FCSTD DOCUMENT  (FreeCAD 2022.709R28846 (Git))
Label: Fresnel_Box_Neck_Template
License: Other
objects: Sketcher::SketchObject×1, PartDesign::Body×1
note: 2 computed .brp shape members not serialized (recipe doc carries the construction recipe); baked Part::Feature solids carry a one-line shape summary decoded from their .brp

FEATURE [Sketcher::SketchObject] Sketch
  ArcFitTolerance = 1e-06
  AttachmentSupport = -> [XY_Plane]
  FullyConstrained = true
  MapMode = 5
  Support = -> [XY_Plane]
  TreeRank = 11
  sketch-geometry (16):
    g0: ArcOfCircle [constr] CenterX=-18.0352 CenterY=0 CenterZ=0 NormalX=0 NormalY=0 NormalZ=1 AngleXU=0 Radius=51.9648 StartAngle=2.35619 EndAngle=3.92699
    g1: ArcOfCircle CenterX=-1.39296 CenterY=-19.4282 CenterZ=0 NormalX=0 NormalY=0 NormalZ=1 AngleXU=0 Radius=79.4404 StartAngle=0.785398 EndAngle=2.07829
    g2: ArcOfCircle CenterX=18.0352 CenterY=0 CenterZ=0 NormalX=0 NormalY=0 NormalZ=1 AngleXU=0 Radius=51.9648 StartAngle=5.49779 EndAngle=7.06858
    g3: ArcOfCircle CenterX=-1.39296 CenterY=19.4282 CenterZ=0 NormalX=0 NormalY=0 NormalZ=1 AngleXU=0 Radius=79.4404 StartAngle=4.2049 EndAngle=5.49779
    g4: LineSegment [constr] StartX=-18.0352 StartY=0 StartZ=0 EndX=18.0352 EndY=0 EndZ=0
    g5: LineSegment [constr] StartX=0 StartY=0 StartZ=0 EndX=0 EndY=60 EndZ=0
    g6: LineSegment [constr] StartX=0 StartY=0 StartZ=0 EndX=0 EndY=-60 EndZ=0
    g7: LineSegment [constr] StartX=-18.0352 StartY=0 StartZ=0 EndX=-70 EndY=0 EndZ=0
    g8: LineSegment [constr] StartX=18.0352 StartY=0 StartZ=0 EndX=70 EndY=0 EndZ=0
    g9: LineSegment StartX=-102.5 StartY=97.5 StartZ=0 EndX=102.5 EndY=97.5 EndZ=0
    g10: LineSegment StartX=102.5 StartY=97.5 StartZ=0 EndX=102.5 EndY=-97.5 EndZ=0
    g11: LineSegment StartX=102.5 StartY=-97.5 StartZ=0 EndX=-102.5 EndY=-97.5 EndZ=0
    g12: LineSegment StartX=-102.5 StartY=-97.5 StartZ=0 EndX=-102.5 EndY=-50 EndZ=0
    g13: LineSegment StartX=-40 StartY=50 StartZ=0 EndX=-102.5 EndY=50 EndZ=0
    g14: LineSegment StartX=-40 StartY=-50 StartZ=0 EndX=-102.5 EndY=-50 EndZ=0
    g15: LineSegment StartX=-102.5 StartY=50 StartZ=0 EndX=-102.5 EndY=97.5 EndZ=0
  constraints (46):
    c: Tangent(g1,g2) = -1.5708
    c: Tangent(g2,g3) = -1.5708
    c: Horizontal(g0,g2)
    c: Coincident(g4,g0)
    c: Coincident(g4,g2)
    c: PointOnObject(g5,g1)
    c: Vertical(g5)
    c: Coincident(g6,g5)
    c: PointOnObject(g6,g3)
    c: Symmetric(g0,g2,g5)
    c: Symmetric(g5,g6,g5)
    c: Equal(g2,g0)
    c: Coincident(g5,g-1)
    c: DistanceY(g6,g5) = 120
    c: Coincident(g7,g0)
    c: PointOnObject(g7,g0)
    c: Horizontal(g7)
    c: Coincident(g8,g2)
    c: PointOnObject(g8,g2)
    c: Horizontal(g8)
    c: DistanceX(g7,g8) = 140
    c: Angle(g2) = 1.5708
    c: Coincident(g9,g10)
    c: Coincident(g10,g11)
    c: Coincident(g11,g12)
    c: Coincident(g15,g9)
    c: Horizontal(g9)
    c: Horizontal(g11)
    c: Vertical(g10)
    c: Vertical(g12)
    c: DistanceX(g9,g9) = 205
    c: DistanceY(g10,g10) = 195
    c: Symmetric(g9,g10,g5)
    c: Horizontal(g13)
    c: Horizontal(g14)
    c: Symmetric(g14,g13,g-1)
    c: DistanceY(g14,g13) = 100
    c: PointOnObject(g12,g14)
    c: Coincident(g15,g13)
    c: Tangent(g12,g15)
    c: Coincident(g1,g13)
    c: Coincident(g3,g14)
    c: DistanceX(g1,g-1) = 40
    c: Equal(g14,g13)
    c: Horizontal(g0,g1)
    c: Horizontal(g0,g2)
FEATURE [PartDesign::Body] Body
  AutoGroupSolids = false
  ClaimAllChildren = false
  ExportMode = 0
  Group = -> [Sketch]
  Origin = -> Origin
  TreeRank = 10
  _ExportChildren = -> [Sketch]
  _GroupVersion = 1
